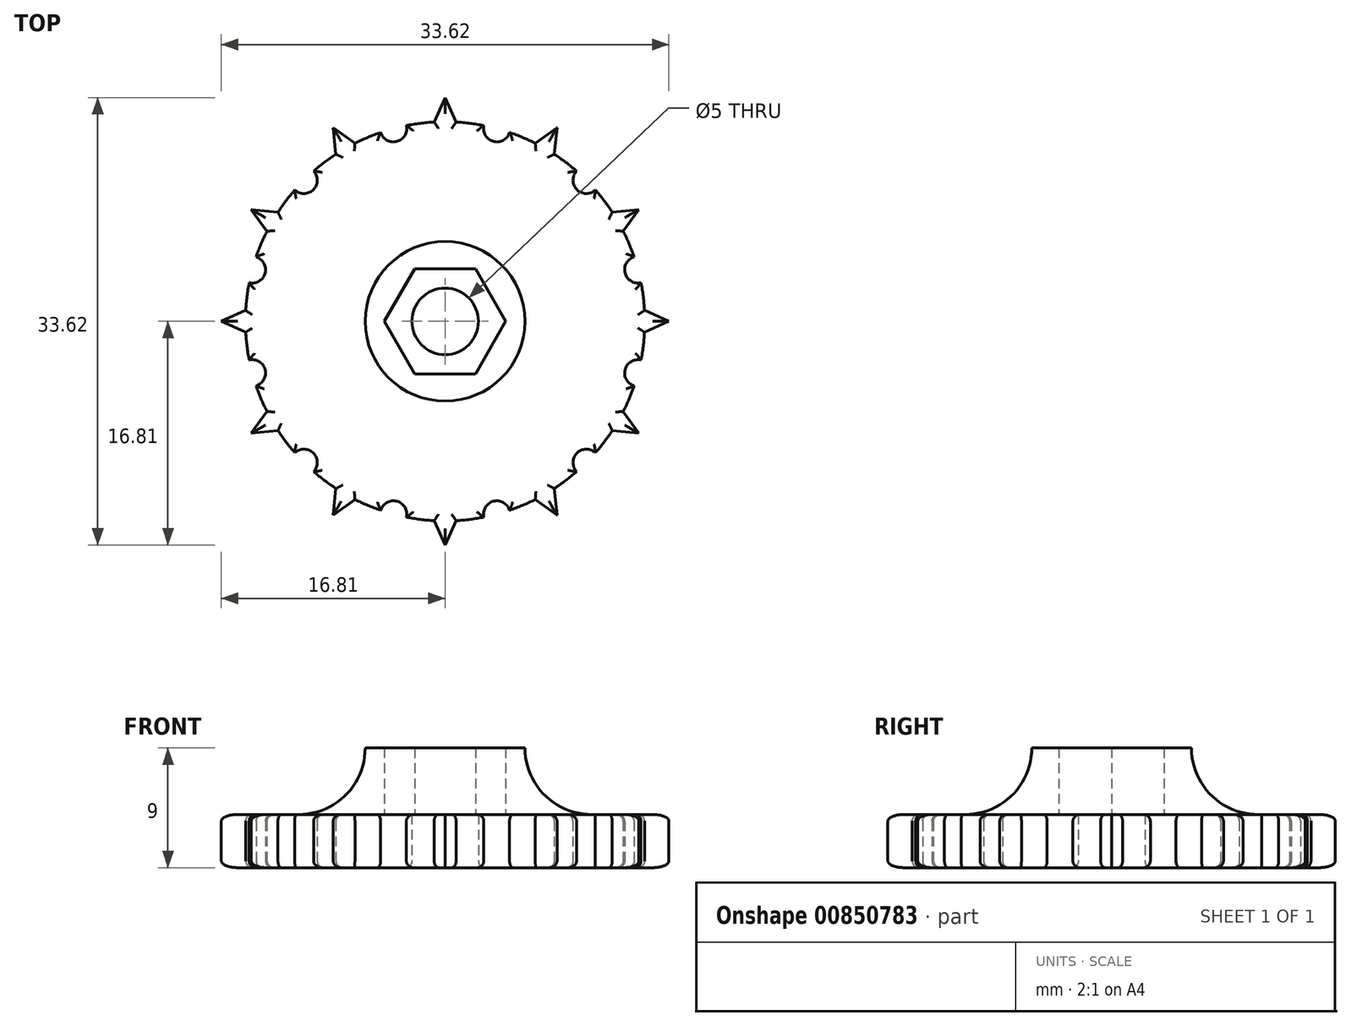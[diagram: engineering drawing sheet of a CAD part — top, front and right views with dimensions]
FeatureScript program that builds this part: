
annotation { "Feature Type Name" : "Feature", "Feature Type Description" : "" }
export const myFeature = defineFeature(function(context is Context, id is Id, definition is map)
    precondition{}
    {
        {
            var Q0;
            Q0=qCreatedBy(makeId("Top.planeOp"),FACE);
            var sketch = newSketch(context, id + "F0", { "sketchPlane" : qUnion([Q0])});
            skArc(sketch, "E0", {"start": v(0, 2.5) * mm, "mid": v(-1.77, 1.77) * mm, "end": v(-2.5, 0) * mm});
            skArc(sketch, "E1", {"start": v(-0.82, 14.98) * mm, "mid": v(-1.87, 14.88) * mm, "end": v(-2.9, 14.72) * mm});
            skLineSegment(sketch, "E2.MirrorCS", {"start": v(0, 16.8) * mm, "end": v(-0.82, 14.98) * mm});
            skLineSegment(sketch, "E3.1.0", {"start": v(-8.4, 14.56) * mm, "end": v(-8.2, 12.56) * mm});
            skLineSegment(sketch, "E3.1.2", {"start": v(-8.4, 14.56) * mm, "end": v(-6.77, 13.38) * mm});
            skLineSegment(sketch, "E3.2.0", {"start": v(-14.56, 8.4) * mm, "end": v(-13.38, 6.77) * mm});
            skLineSegment(sketch, "E3.2.2", {"start": v(-14.56, 8.4) * mm, "end": v(-12.56, 8.2) * mm});
            skLineSegment(sketch, "E3.3.2", {"start": v(-16.8, 0) * mm, "end": v(-14.98, 0.82) * mm});
            skArc(sketch, "E4", {"start": v(-4.84, 14.2) * mm, "mid": v(-3.62, 13.52) * mm, "end": v(-2.9, 14.72) * mm});
            skArc(sketch, "E5.1.0", {"start": v(-11.29, 9.88) * mm, "mid": v(-9.9, 9.9) * mm, "end": v(-9.88, 11.29) * mm});
            skArc(sketch, "E5.2.0", {"start": v(-14.72, 2.9) * mm, "mid": v(-13.52, 3.62) * mm, "end": v(-14.2, 4.84) * mm});
            skLineSegment(sketch, "E6", {"start": v(0, 18.11) * mm, "end": v(0, 0) * mm, "construction": true});
            skLineSegment(sketch, "E7", {"start": v(-23.78, 0) * mm, "end": v(0, 0) * mm, "construction": true});
            skArc(sketch, "E8.trimOffspring", {"start": v(-13.38, 6.77) * mm, "mid": v(-13.82, 5.82) * mm, "end": v(-14.2, 4.84) * mm});
            skArc(sketch, "E9.trimOffspring", {"start": v(-14.72, 2.9) * mm, "mid": v(-14.88, 1.87) * mm, "end": v(-14.98, 0.82) * mm});
            skArc(sketch, "E10.trimOffspring", {"start": v(-11.29, 9.88) * mm, "mid": v(-11.95, 9.06) * mm, "end": v(-12.56, 8.2) * mm});
            skArc(sketch, "E11.trimOffspring", {"start": v(-4.84, 14.2) * mm, "mid": v(-5.82, 13.82) * mm, "end": v(-6.77, 13.38) * mm});
            skArc(sketch, "E12.trimOffspring", {"start": v(-8.2, 12.56) * mm, "mid": v(-9.06, 11.95) * mm, "end": v(-9.88, 11.29) * mm});
            skPoint(sketch, "E13.start.orphan", {"position": v(-3.76, 14.04) * mm});
            skPoint(sketch, "E14.trimOffspring.end.orphan", {"position": v(-0.9, 14.8) * mm});
            skPoint(sketch, "E15.orphan", {"position": v(-6.63, 13.27) * mm});
            skArc(sketch, "E16.MirrorCS", {"start": v(0.82, 14.98) * mm, "mid": v(1.87, 14.88) * mm, "end": v(2.9, 14.72) * mm});
            skArc(sketch, "E17.MirrorCS", {"start": v(4.84, 14.2) * mm, "mid": v(5.82, 13.82) * mm, "end": v(6.77, 13.38) * mm});
            skLineSegment(sketch, "E18.MirrorCS", {"start": v(8.4, 14.56) * mm, "end": v(8.2, 12.56) * mm});
            skLineSegment(sketch, "E19.MirrorCS", {"start": v(8.4, 14.56) * mm, "end": v(6.77, 13.38) * mm});
            skArc(sketch, "E20.MirrorCS", {"start": v(13.38, 6.77) * mm, "mid": v(13.82, 5.82) * mm, "end": v(14.2, 4.84) * mm});
            skLineSegment(sketch, "E21.MirrorCS", {"start": v(14.56, 8.4) * mm, "end": v(12.56, 8.2) * mm});
            skLineSegment(sketch, "E22.MirrorCS", {"start": v(14.56, 8.4) * mm, "end": v(13.38, 6.77) * mm});
            skArc(sketch, "E23.MirrorCS", {"start": v(11.29, 9.88) * mm, "mid": v(11.95, 9.06) * mm, "end": v(12.56, 8.2) * mm});
            skArc(sketch, "E24.MirrorCS", {"start": v(14.72, 2.9) * mm, "mid": v(14.88, 1.87) * mm, "end": v(14.98, 0.82) * mm});
            skArc(sketch, "E25.MirrorCS", {"start": v(8.2, 12.56) * mm, "mid": v(9.06, 11.95) * mm, "end": v(9.88, 11.29) * mm});
            skLineSegment(sketch, "E26.MirrorCS", {"start": v(0, 16.8) * mm, "end": v(0.82, 14.98) * mm});
            skArc(sketch, "E27.MirrorCS", {"start": v(4.84, 14.2) * mm, "mid": v(3.62, 13.52) * mm, "end": v(2.9, 14.72) * mm});
            skLineSegment(sketch, "E28.MirrorCS", {"start": v(16.8, 0) * mm, "end": v(14.98, 0.82) * mm});
            skArc(sketch, "E29.MirrorCS", {"start": v(11.29, 9.88) * mm, "mid": v(9.9, 9.9) * mm, "end": v(9.88, 11.29) * mm});
            skArc(sketch, "E30.MirrorCS", {"start": v(14.72, 2.9) * mm, "mid": v(13.52, 3.62) * mm, "end": v(14.2, 4.84) * mm});
            skLineSegment(sketch, "E31.MirrorCS", {"start": v(23.78, 0) * mm, "end": v(0, 0) * mm, "construction": true});
            skPoint(sketch, "E32.MirrorP", {"position": v(3.76, 14.04) * mm});
            skPoint(sketch, "E33.MirrorP", {"position": v(6.63, 13.27) * mm});
            skArc(sketch, "E34.MirrorCS", {"start": v(0, 2.5) * mm, "mid": v(1.77, 1.77) * mm, "end": v(2.5, 0) * mm});
            skPoint(sketch, "E35.MirrorP", {"position": v(0.9, 14.8) * mm});
            skArc(sketch, "E36.MirrorCS", {"start": v(-13.38, -6.77) * mm, "mid": v(-13.82, -5.82) * mm, "end": v(-14.2, -4.84) * mm});
            skLineSegment(sketch, "E37.MirrorCS", {"start": v(0, -16.8) * mm, "end": v(-0.82, -14.98) * mm});
            skArc(sketch, "E38.MirrorCS", {"start": v(-8.2, -12.56) * mm, "mid": v(-9.06, -11.95) * mm, "end": v(-9.88, -11.29) * mm});
            skLineSegment(sketch, "E39.MirrorCS", {"start": v(-14.56, -8.4) * mm, "end": v(-13.38, -6.77) * mm});
            skArc(sketch, "E40.MirrorCS", {"start": v(4.84, -14.2) * mm, "mid": v(5.82, -13.82) * mm, "end": v(6.77, -13.38) * mm});
            skLineSegment(sketch, "E41.MirrorCS", {"start": v(-8.4, -14.56) * mm, "end": v(-8.2, -12.56) * mm});
            skLineSegment(sketch, "E42.MirrorCS", {"start": v(-14.56, -8.4) * mm, "end": v(-12.56, -8.2) * mm});
            skLineSegment(sketch, "E43.MirrorCS", {"start": v(8.4, -14.56) * mm, "end": v(6.77, -13.38) * mm});
            skArc(sketch, "E44.MirrorCS", {"start": v(-0.82, -14.98) * mm, "mid": v(-1.87, -14.88) * mm, "end": v(-2.9, -14.72) * mm});
            skLineSegment(sketch, "E45.MirrorCS", {"start": v(14.56, -8.4) * mm, "end": v(13.38, -6.77) * mm});
            skArc(sketch, "E46.MirrorCS", {"start": v(-4.84, -14.2) * mm, "mid": v(-3.62, -13.52) * mm, "end": v(-2.9, -14.72) * mm});
            skArc(sketch, "E47.MirrorCS", {"start": v(14.72, -2.9) * mm, "mid": v(14.88, -1.87) * mm, "end": v(14.98, -0.82) * mm});
            skLineSegment(sketch, "E48.MirrorCS", {"start": v(0, -16.8) * mm, "end": v(0.82, -14.98) * mm});
            skLineSegment(sketch, "E49.MirrorCS", {"start": v(14.56, -8.4) * mm, "end": v(12.56, -8.2) * mm});
            skArc(sketch, "E50.MirrorCS", {"start": v(8.2, -12.56) * mm, "mid": v(9.06, -11.95) * mm, "end": v(9.88, -11.29) * mm});
            skArc(sketch, "E51.MirrorCS", {"start": v(11.29, -9.88) * mm, "mid": v(11.95, -9.06) * mm, "end": v(12.56, -8.2) * mm});
            skArc(sketch, "E52.MirrorCS", {"start": v(13.38, -6.77) * mm, "mid": v(13.82, -5.82) * mm, "end": v(14.2, -4.84) * mm});
            skArc(sketch, "E53.MirrorCS", {"start": v(-14.72, -2.9) * mm, "mid": v(-14.88, -1.87) * mm, "end": v(-14.98, -0.82) * mm});
            skLineSegment(sketch, "E54.MirrorCS", {"start": v(8.4, -14.56) * mm, "end": v(8.2, -12.56) * mm});
            skArc(sketch, "E55.MirrorCS", {"start": v(-11.29, -9.88) * mm, "mid": v(-11.95, -9.06) * mm, "end": v(-12.56, -8.2) * mm});
            skArc(sketch, "E56.MirrorCS", {"start": v(-4.84, -14.2) * mm, "mid": v(-5.82, -13.82) * mm, "end": v(-6.77, -13.38) * mm});
            skLineSegment(sketch, "E57.MirrorCS", {"start": v(-8.4, -14.56) * mm, "end": v(-6.77, -13.38) * mm});
            skArc(sketch, "E58.MirrorCS", {"start": v(0.82, -14.98) * mm, "mid": v(1.87, -14.88) * mm, "end": v(2.9, -14.72) * mm});
            skLineSegment(sketch, "E59.MirrorCS", {"start": v(16.8, 0) * mm, "end": v(14.98, -0.82) * mm});
            skLineSegment(sketch, "E60.MirrorCS", {"start": v(-16.8, 0) * mm, "end": v(-14.98, -0.82) * mm});
            skArc(sketch, "E61.MirrorCS", {"start": v(-11.29, -9.88) * mm, "mid": v(-9.9, -9.9) * mm, "end": v(-9.88, -11.29) * mm});
            skArc(sketch, "E62.MirrorCS", {"start": v(4.84, -14.2) * mm, "mid": v(3.62, -13.52) * mm, "end": v(2.9, -14.72) * mm});
            skPoint(sketch, "E63.MirrorP", {"position": v(0.9, -14.8) * mm});
            skArc(sketch, "E64.MirrorCS", {"start": v(0, -2.5) * mm, "mid": v(1.77, -1.77) * mm, "end": v(2.5, 0) * mm});
            skArc(sketch, "E65.MirrorCS", {"start": v(0, -2.5) * mm, "mid": v(-1.77, -1.77) * mm, "end": v(-2.5, 0) * mm});
            skPoint(sketch, "E66.MirrorP", {"position": v(-0.9, -14.8) * mm});
            skPoint(sketch, "E67.MirrorP", {"position": v(6.63, -13.27) * mm});
            skArc(sketch, "E68.MirrorCS", {"start": v(-14.72, -2.9) * mm, "mid": v(-13.52, -3.62) * mm, "end": v(-14.2, -4.84) * mm});
            skPoint(sketch, "E69.MirrorP", {"position": v(3.76, -14.04) * mm});
            skLineSegment(sketch, "E70.MirrorCS", {"start": v(0, -18.11) * mm, "end": v(0, 0) * mm, "construction": true});
            skPoint(sketch, "E71.MirrorP", {"position": v(-3.76, -14.04) * mm});
            skArc(sketch, "E72.MirrorCS", {"start": v(11.29, -9.88) * mm, "mid": v(9.9, -9.9) * mm, "end": v(9.88, -11.29) * mm});
            skArc(sketch, "E73.MirrorCS", {"start": v(14.72, -2.9) * mm, "mid": v(13.52, -3.62) * mm, "end": v(14.2, -4.84) * mm});
            skPoint(sketch, "E74.MirrorP", {"position": v(-6.63, -13.27) * mm});
            skSolve(sketch);
        }
        {
            var Q0;
            Q0=qSketchRegion(id+"F0",true);
            extrude(context, id + "F1", {"entities" : qUnion([Q0]), "depth" : 4 * mm, "offsetDistance" : 25 * mm});
        }
        {
            var Q0;
            Q0=makeQuery(id+"F1.opExtrude","CAP_FACE",FACE,{"disambiguationData":[OSD([sQuery(id+"F0.wireOp",EDGE,"E0"),sQuery(id+"F0.wireOp",EDGE,"E1"),sQuery(id+"F0.wireOp",EDGE,"E2.MirrorCS"),sQuery(id+"F0.wireOp",EDGE,"E3.1.0"),sQuery(id+"F0.wireOp",EDGE,"E3.1.2"),sQuery(id+"F0.wireOp",EDGE,"E3.2.0"),sQuery(id+"F0.wireOp",EDGE,"E3.2.2"),sQuery(id+"F0.wireOp",EDGE,"E3.3.2"),sQuery(id+"F0.wireOp",EDGE,"E4"),sQuery(id+"F0.wireOp",EDGE,"E5.1.0"),sQuery(id+"F0.wireOp",EDGE,"E5.2.0"),sQuery(id+"F0.wireOp",EDGE,"E8.trimOffspring"),sQuery(id+"F0.wireOp",EDGE,"E9.trimOffspring"),sQuery(id+"F0.wireOp",EDGE,"E10.trimOffspring"),sQuery(id+"F0.wireOp",EDGE,"E11.trimOffspring"),sQuery(id+"F0.wireOp",EDGE,"E12.trimOffspring"),sQuery(id+"F0.wireOp",EDGE,"E16.MirrorCS"),sQuery(id+"F0.wireOp",EDGE,"E17.MirrorCS"),sQuery(id+"F0.wireOp",EDGE,"E18.MirrorCS"),sQuery(id+"F0.wireOp",EDGE,"E19.MirrorCS"),sQuery(id+"F0.wireOp",EDGE,"E20.MirrorCS"),sQuery(id+"F0.wireOp",EDGE,"E21.MirrorCS"),sQuery(id+"F0.wireOp",EDGE,"E22.MirrorCS"),sQuery(id+"F0.wireOp",EDGE,"E23.MirrorCS"),sQuery(id+"F0.wireOp",EDGE,"E24.MirrorCS"),sQuery(id+"F0.wireOp",EDGE,"E25.MirrorCS"),sQuery(id+"F0.wireOp",EDGE,"E26.MirrorCS"),sQuery(id+"F0.wireOp",EDGE,"E27.MirrorCS"),sQuery(id+"F0.wireOp",EDGE,"E28.MirrorCS"),sQuery(id+"F0.wireOp",EDGE,"E29.MirrorCS"),sQuery(id+"F0.wireOp",EDGE,"E30.MirrorCS"),sQuery(id+"F0.wireOp",EDGE,"E34.MirrorCS"),sQuery(id+"F0.wireOp",EDGE,"E36.MirrorCS"),sQuery(id+"F0.wireOp",EDGE,"E37.MirrorCS"),sQuery(id+"F0.wireOp",EDGE,"E38.MirrorCS"),sQuery(id+"F0.wireOp",EDGE,"E39.MirrorCS"),sQuery(id+"F0.wireOp",EDGE,"E40.MirrorCS"),sQuery(id+"F0.wireOp",EDGE,"E41.MirrorCS"),sQuery(id+"F0.wireOp",EDGE,"E42.MirrorCS"),sQuery(id+"F0.wireOp",EDGE,"E43.MirrorCS"),sQuery(id+"F0.wireOp",EDGE,"E44.MirrorCS"),sQuery(id+"F0.wireOp",EDGE,"E45.MirrorCS"),sQuery(id+"F0.wireOp",EDGE,"E46.MirrorCS"),sQuery(id+"F0.wireOp",EDGE,"E47.MirrorCS"),sQuery(id+"F0.wireOp",EDGE,"E48.MirrorCS"),sQuery(id+"F0.wireOp",EDGE,"E49.MirrorCS"),sQuery(id+"F0.wireOp",EDGE,"E50.MirrorCS"),sQuery(id+"F0.wireOp",EDGE,"E51.MirrorCS"),sQuery(id+"F0.wireOp",EDGE,"E52.MirrorCS"),sQuery(id+"F0.wireOp",EDGE,"E53.MirrorCS"),sQuery(id+"F0.wireOp",EDGE,"E54.MirrorCS"),sQuery(id+"F0.wireOp",EDGE,"E55.MirrorCS"),sQuery(id+"F0.wireOp",EDGE,"E56.MirrorCS"),sQuery(id+"F0.wireOp",EDGE,"E57.MirrorCS"),sQuery(id+"F0.wireOp",EDGE,"E58.MirrorCS"),sQuery(id+"F0.wireOp",EDGE,"E59.MirrorCS"),sQuery(id+"F0.wireOp",EDGE,"E60.MirrorCS"),sQuery(id+"F0.wireOp",EDGE,"E61.MirrorCS"),sQuery(id+"F0.wireOp",EDGE,"E62.MirrorCS"),sQuery(id+"F0.wireOp",EDGE,"E64.MirrorCS"),sQuery(id+"F0.wireOp",EDGE,"E65.MirrorCS"),sQuery(id+"F0.wireOp",EDGE,"E68.MirrorCS"),sQuery(id+"F0.wireOp",EDGE,"E72.MirrorCS"),sQuery(id+"F0.wireOp",EDGE,"E73.MirrorCS")])],"isStart":false});
            var sketch = newSketch(context, id + "F2", { "sketchPlane" : qUnion([Q0])});
            skCircle(sketch, "E75.cCircle", {"center": v(0, 0) * mm, "radius": 3.95 * mm, "construction": true});
            skLineSegment(sketch, "E75.0", {"start": v(-2.28, 3.95) * mm, "end": v(2.28, 3.95) * mm});
            skLineSegment(sketch, "E75.1", {"start": v(2.28, 3.95) * mm, "end": v(4.56, 0) * mm});
            skLineSegment(sketch, "E75.2", {"start": v(4.56, 0) * mm, "end": v(2.28, -3.95) * mm});
            skLineSegment(sketch, "E75.3", {"start": v(2.28, -3.95) * mm, "end": v(-2.28, -3.95) * mm});
            skLineSegment(sketch, "E75.4", {"start": v(-2.28, -3.95) * mm, "end": v(-4.56, 0) * mm});
            skLineSegment(sketch, "E75.5", {"start": v(-4.56, 0) * mm, "end": v(-2.28, 3.95) * mm});
            skPoint(sketch, "E75.0.midPoint", {"position": v(0, 3.95) * mm});
            skCircle(sketch, "E76", {"center": v(0, 0) * mm, "radius": 6 * mm});
            skSolve(sketch);
        }
        {
            var Q0;
            Q0=qSketchRegion(id+"F2",true);
            extrude(context, id + "F3", {"entities" : qUnion([Q0]), "operationType" : NewBodyOperationType.ADD, "depth" : 5 * mm, "offsetDistance" : 25 * mm});
        }
        {
            var Q0;
            Q0=makeQuery(id+"F3.opExtrude","CAP_EDGE",EDGE,{"disambiguationData":[OSD([sQuery(id+"F2.wireOp",EDGE,"E76")])],"isStart":true});
            fillet(context, id + "F4", {"entities" : qUnion([Q0]), "radius" : 5 * mm, "tangentPropagation" : true, "allowEdgeOverflow" : false});
        }
        {
            var Q0;
            {var subQ0=sQuery(id+"F0.wireOp",EDGE,"E51.MirrorCS");var subQ1=sQuery(id+"F0.wireOp",EDGE,"E50.MirrorCS");var subQ2=sQuery(id+"F0.wireOp",EDGE,"E49.MirrorCS");var subQ3=sQuery(id+"F0.wireOp",EDGE,"E48.MirrorCS");var subQ4=sQuery(id+"F0.wireOp",EDGE,"E47.MirrorCS");var subQ5=sQuery(id+"F0.wireOp",EDGE,"E46.MirrorCS");var subQ6=sQuery(id+"F0.wireOp",EDGE,"E45.MirrorCS");var subQ7=sQuery(id+"F0.wireOp",EDGE,"E44.MirrorCS");var subQ8=sQuery(id+"F0.wireOp",EDGE,"E43.MirrorCS");var subQ9=sQuery(id+"F0.wireOp",EDGE,"E42.MirrorCS");var subQ10=sQuery(id+"F0.wireOp",EDGE,"E41.MirrorCS");var subQ11=sQuery(id+"F0.wireOp",EDGE,"E40.MirrorCS");var subQ12=sQuery(id+"F0.wireOp",EDGE,"E39.MirrorCS");var subQ13=sQuery(id+"F0.wireOp",EDGE,"E38.MirrorCS");var subQ14=sQuery(id+"F0.wireOp",EDGE,"E37.MirrorCS");var subQ15=sQuery(id+"F0.wireOp",EDGE,"E36.MirrorCS");var subQ16=sQuery(id+"F0.wireOp",EDGE,"E30.MirrorCS");var subQ17=sQuery(id+"F0.wireOp",EDGE,"E29.MirrorCS");var subQ18=sQuery(id+"F0.wireOp",EDGE,"E28.MirrorCS");var subQ19=sQuery(id+"F0.wireOp",EDGE,"E27.MirrorCS");var subQ20=sQuery(id+"F0.wireOp",EDGE,"E26.MirrorCS");var subQ21=sQuery(id+"F0.wireOp",EDGE,"E25.MirrorCS");var subQ22=sQuery(id+"F0.wireOp",EDGE,"E24.MirrorCS");var subQ23=sQuery(id+"F0.wireOp",EDGE,"E23.MirrorCS");var subQ24=sQuery(id+"F0.wireOp",EDGE,"E5.2.0");var subQ25=sQuery(id+"F0.wireOp",EDGE,"E5.1.0");var subQ26=sQuery(id+"F0.wireOp",EDGE,"E4");var subQ27=sQuery(id+"F0.wireOp",EDGE,"E3.3.2");var subQ28=sQuery(id+"F0.wireOp",EDGE,"E3.2.2");var subQ29=sQuery(id+"F0.wireOp",EDGE,"E3.2.0");var subQ30=sQuery(id+"F0.wireOp",EDGE,"E1");var subQ31=sQuery(id+"F0.wireOp",EDGE,"E2.MirrorCS");var subQ32=sQuery(id+"F0.wireOp",EDGE,"E3.1.0");var subQ33=sQuery(id+"F0.wireOp",EDGE,"E3.1.2");var subQ34=sQuery(id+"F0.wireOp",EDGE,"E8.trimOffspring");var subQ35=sQuery(id+"F0.wireOp",EDGE,"E9.trimOffspring");var subQ36=sQuery(id+"F0.wireOp",EDGE,"E10.trimOffspring");var subQ37=sQuery(id+"F0.wireOp",EDGE,"E11.trimOffspring");var subQ38=sQuery(id+"F0.wireOp",EDGE,"E12.trimOffspring");var subQ39=sQuery(id+"F0.wireOp",EDGE,"E16.MirrorCS");var subQ40=sQuery(id+"F0.wireOp",EDGE,"E17.MirrorCS");var subQ41=sQuery(id+"F0.wireOp",EDGE,"E18.MirrorCS");var subQ42=sQuery(id+"F0.wireOp",EDGE,"E19.MirrorCS");var subQ43=sQuery(id+"F0.wireOp",EDGE,"E20.MirrorCS");var subQ44=sQuery(id+"F0.wireOp",EDGE,"E21.MirrorCS");var subQ45=sQuery(id+"F0.wireOp",EDGE,"E22.MirrorCS");var subQ46=sQuery(id+"F0.wireOp",EDGE,"E52.MirrorCS");var subQ47=sQuery(id+"F0.wireOp",EDGE,"E53.MirrorCS");var subQ48=sQuery(id+"F0.wireOp",EDGE,"E54.MirrorCS");var subQ49=sQuery(id+"F0.wireOp",EDGE,"E55.MirrorCS");var subQ50=sQuery(id+"F0.wireOp",EDGE,"E56.MirrorCS");var subQ51=sQuery(id+"F0.wireOp",EDGE,"E57.MirrorCS");var subQ52=sQuery(id+"F0.wireOp",EDGE,"E58.MirrorCS");var subQ53=sQuery(id+"F0.wireOp",EDGE,"E59.MirrorCS");var subQ54=sQuery(id+"F0.wireOp",EDGE,"E60.MirrorCS");var subQ55=sQuery(id+"F0.wireOp",EDGE,"E61.MirrorCS");var subQ56=sQuery(id+"F0.wireOp",EDGE,"E62.MirrorCS");var subQ57=sQuery(id+"F0.wireOp",EDGE,"E68.MirrorCS");var subQ58=sQuery(id+"F0.wireOp",EDGE,"E72.MirrorCS");var subQ59=sQuery(id+"F0.wireOp",EDGE,"E73.MirrorCS");Q0=makeQuery(id+"F3.boolean.opBoolean","SPLIT",FACE,{"disambiguationData":[TD([makeQuery(id+"F1.opExtrude","SWEPT_FACE",FACE,{"disambiguationData":[OSD([subQ30])]})])],"derivedFrom":makeQuery(id+"F1.opExtrude","CAP_FACE",FACE,{"disambiguationData":[OSD([sQuery(id+"F0.wireOp",EDGE,"E0"),subQ30,subQ31,subQ32,subQ33,subQ29,subQ28,subQ27,subQ26,subQ25,subQ24,subQ34,subQ35,subQ36,subQ37,subQ38,subQ39,subQ40,subQ41,subQ42,subQ43,subQ44,subQ45,subQ23,subQ22,subQ21,subQ20,subQ19,subQ18,subQ17,subQ16,sQuery(id+"F0.wireOp",EDGE,"E34.MirrorCS"),subQ15,subQ14,subQ13,subQ12,subQ11,subQ10,subQ9,subQ8,subQ7,subQ6,subQ5,subQ4,subQ3,subQ2,subQ1,subQ0,subQ46,subQ47,subQ48,subQ49,subQ50,subQ51,subQ52,subQ53,subQ54,subQ55,subQ56,sQuery(id+"F0.wireOp",EDGE,"E64.MirrorCS"),sQuery(id+"F0.wireOp",EDGE,"E65.MirrorCS"),subQ57,subQ58,subQ59])],"isStart":false})});}
            var Q1;
            Q1=makeQuery(id+"F1.opExtrude","CAP_FACE",FACE,{"disambiguationData":[OSD([sQuery(id+"F0.wireOp",EDGE,"E0"),sQuery(id+"F0.wireOp",EDGE,"E1"),sQuery(id+"F0.wireOp",EDGE,"E2.MirrorCS"),sQuery(id+"F0.wireOp",EDGE,"E3.1.0"),sQuery(id+"F0.wireOp",EDGE,"E3.1.2"),sQuery(id+"F0.wireOp",EDGE,"E3.2.0"),sQuery(id+"F0.wireOp",EDGE,"E3.2.2"),sQuery(id+"F0.wireOp",EDGE,"E3.3.2"),sQuery(id+"F0.wireOp",EDGE,"E4"),sQuery(id+"F0.wireOp",EDGE,"E5.1.0"),sQuery(id+"F0.wireOp",EDGE,"E5.2.0"),sQuery(id+"F0.wireOp",EDGE,"E8.trimOffspring"),sQuery(id+"F0.wireOp",EDGE,"E9.trimOffspring"),sQuery(id+"F0.wireOp",EDGE,"E10.trimOffspring"),sQuery(id+"F0.wireOp",EDGE,"E11.trimOffspring"),sQuery(id+"F0.wireOp",EDGE,"E12.trimOffspring"),sQuery(id+"F0.wireOp",EDGE,"E16.MirrorCS"),sQuery(id+"F0.wireOp",EDGE,"E17.MirrorCS"),sQuery(id+"F0.wireOp",EDGE,"E18.MirrorCS"),sQuery(id+"F0.wireOp",EDGE,"E19.MirrorCS"),sQuery(id+"F0.wireOp",EDGE,"E20.MirrorCS"),sQuery(id+"F0.wireOp",EDGE,"E21.MirrorCS"),sQuery(id+"F0.wireOp",EDGE,"E22.MirrorCS"),sQuery(id+"F0.wireOp",EDGE,"E23.MirrorCS"),sQuery(id+"F0.wireOp",EDGE,"E24.MirrorCS"),sQuery(id+"F0.wireOp",EDGE,"E25.MirrorCS"),sQuery(id+"F0.wireOp",EDGE,"E26.MirrorCS"),sQuery(id+"F0.wireOp",EDGE,"E27.MirrorCS"),sQuery(id+"F0.wireOp",EDGE,"E28.MirrorCS"),sQuery(id+"F0.wireOp",EDGE,"E29.MirrorCS"),sQuery(id+"F0.wireOp",EDGE,"E30.MirrorCS"),sQuery(id+"F0.wireOp",EDGE,"E34.MirrorCS"),sQuery(id+"F0.wireOp",EDGE,"E36.MirrorCS"),sQuery(id+"F0.wireOp",EDGE,"E37.MirrorCS"),sQuery(id+"F0.wireOp",EDGE,"E38.MirrorCS"),sQuery(id+"F0.wireOp",EDGE,"E39.MirrorCS"),sQuery(id+"F0.wireOp",EDGE,"E40.MirrorCS"),sQuery(id+"F0.wireOp",EDGE,"E41.MirrorCS"),sQuery(id+"F0.wireOp",EDGE,"E42.MirrorCS"),sQuery(id+"F0.wireOp",EDGE,"E43.MirrorCS"),sQuery(id+"F0.wireOp",EDGE,"E44.MirrorCS"),sQuery(id+"F0.wireOp",EDGE,"E45.MirrorCS"),sQuery(id+"F0.wireOp",EDGE,"E46.MirrorCS"),sQuery(id+"F0.wireOp",EDGE,"E47.MirrorCS"),sQuery(id+"F0.wireOp",EDGE,"E48.MirrorCS"),sQuery(id+"F0.wireOp",EDGE,"E49.MirrorCS"),sQuery(id+"F0.wireOp",EDGE,"E50.MirrorCS"),sQuery(id+"F0.wireOp",EDGE,"E51.MirrorCS"),sQuery(id+"F0.wireOp",EDGE,"E52.MirrorCS"),sQuery(id+"F0.wireOp",EDGE,"E53.MirrorCS"),sQuery(id+"F0.wireOp",EDGE,"E54.MirrorCS"),sQuery(id+"F0.wireOp",EDGE,"E55.MirrorCS"),sQuery(id+"F0.wireOp",EDGE,"E56.MirrorCS"),sQuery(id+"F0.wireOp",EDGE,"E57.MirrorCS"),sQuery(id+"F0.wireOp",EDGE,"E58.MirrorCS"),sQuery(id+"F0.wireOp",EDGE,"E59.MirrorCS"),sQuery(id+"F0.wireOp",EDGE,"E60.MirrorCS"),sQuery(id+"F0.wireOp",EDGE,"E61.MirrorCS"),sQuery(id+"F0.wireOp",EDGE,"E62.MirrorCS"),sQuery(id+"F0.wireOp",EDGE,"E64.MirrorCS"),sQuery(id+"F0.wireOp",EDGE,"E65.MirrorCS"),sQuery(id+"F0.wireOp",EDGE,"E68.MirrorCS"),sQuery(id+"F0.wireOp",EDGE,"E72.MirrorCS"),sQuery(id+"F0.wireOp",EDGE,"E73.MirrorCS")])],"isStart":true});
            fillet(context, id + "F5", {"entities" : qUnion([Q0, Q1]), "radius" : 0.5 * mm, "tangentPropagation" : true, "allowEdgeOverflow" : false});
        }
    });
